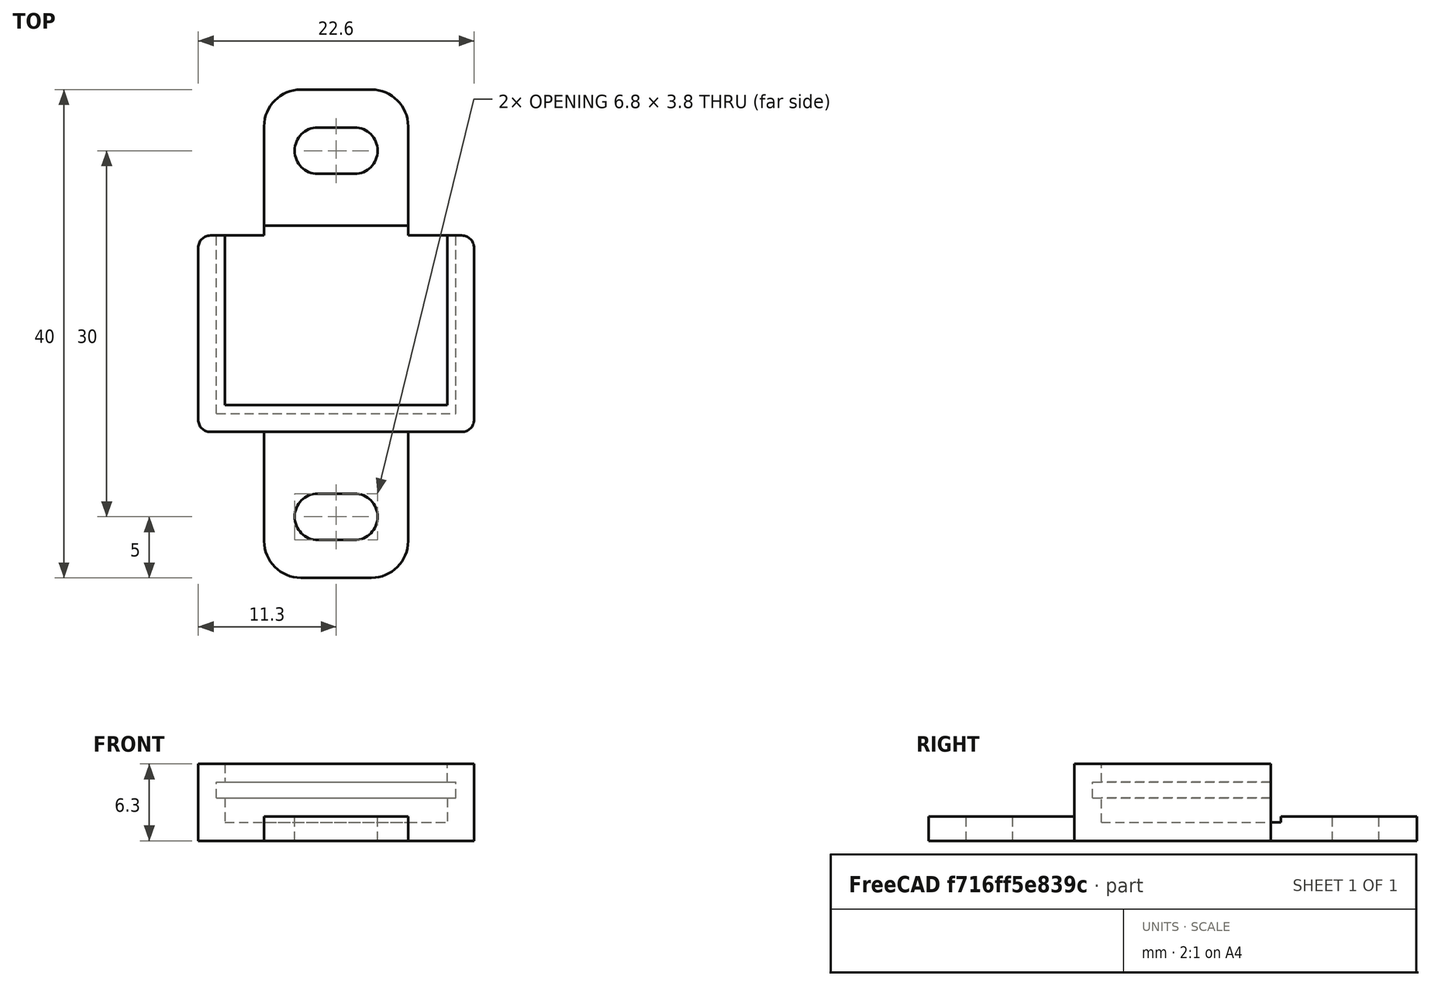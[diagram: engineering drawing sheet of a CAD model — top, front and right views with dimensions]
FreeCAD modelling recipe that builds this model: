
FCSTD DOCUMENT  (FreeCAD 0.19R23578 (Git))
Label: charger_s09
License: FreeArt
LicenseURL: http://artlibre.org/licence/lal
objects: Part::Box×3, Part::MultiFuse×2, Spreadsheet::Sheet×1, Part::Fillet×1, Part::Feature×1, Part::Cut×1, App::Part×1
note: 8 computed .brp shape members not serialized (recipe doc carries the construction recipe); baked Part::Feature solids carry a one-line shape summary decoded from their .brp

FEATURE [Spreadsheet::Sheet] Spreadsheet  label="p"
  cells = A1=pcb_x; B1(pcb_x)=19.6; A2=pcb_y; B2(pcb_y)=14.6; A3=pcb_z; B3(pcb_z)=1.3; A4=pcb_under; B4(pcb_under)=2; A5=side_wall; B5(side_wall)=1.5; A6=pcb_side_lane; B6(pcb_side_lane)=0.7; A7=bottom_wall; B7(bottom_wall)=1.5; A8=pcb_above; B8(pcb_above)=1.5
FEATURE [Part::Box] Box  label="external cube"
  AttacherType = Attacher::AttachEngine3D
  Height = 6.3
  Length = 22.6
  Width = 16.1
  expr: Length = <<p>>.pcb_x + 2 * <<p>>.side_wall
  expr: Width = <<p>>.pcb_y + <<p>>.side_wall
  expr: Height = <<p>>.bottom_wall + <<p>>.pcb_under + <<p>>.pcb_z + <<p>>.pcb_above
FEATURE [Part::Box] Box006  label="internal cube"
  AttacherType = Attacher::AttachEngine3D
  Height = 4.8
  Length = 18.2
  Placement = pos=(2.2,2.2,1.5) rot=(0,0,1;0rad)
  Width = 14.7
  expr: Length = <<p>>.pcb_x - 2 * <<p>>.pcb_side_lane
  expr: Width = <<p>>.pcb_y - 2 * <<p>>.pcb_side_lane + <<p>>.side_wall
  expr: Height = <<p>>.pcb_under + <<p>>.pcb_z + <<p>>.pcb_above
  expr: .Placement.Base.z = <<p>>.bottom_wall
  expr: .Placement.Base.x = <<p>>.side_wall + <<p>>.pcb_side_lane
  expr: .Placement.Base.y = <<p>>.side_wall + <<p>>.pcb_side_lane
FEATURE [Part::Box] Box007  label="pcb extract cube"
  AttacherType = Attacher::AttachEngine3D
  Height = 1.3
  Length = 19.6
  Placement = pos=(1.5,1.5,3.5) rot=(0,0,1;0rad)
  Width = 14.6
  expr: Height = <<p>>.pcb_z
  expr: .Placement.Base.z = <<p>>.bottom_wall + <<p>>.pcb_under
  expr: Width = <<p>>.pcb_y
  expr: Length = <<p>>.pcb_x
  expr: .Placement.Base.x = <<p>>.side_wall
  expr: .Placement.Base.y = <<p>>.side_wall
FEATURE [Part::MultiFuse] Fusion  label="extract fusion"
  Shapes = -> [Box006,Box007]
FEATURE [Part::Fillet] Fillet  label="external fillet"
  Base = -> Box
  Edges = 4 edges r=1: [Edge1,Edge3,Edge5,Edge7]
FEATURE [Part::Feature] Cut002002  label="attach plane y dir002"
  Placement = pos=(5.4,-11.95,0) rot=(0,0,1;0rad)
  shape: bbox 11.8 x 40 x 2 mm, 20 faces (baked)
FEATURE [Part::MultiFuse] Fusion001  label="body fusion"
  Shapes = -> [Fillet,Cut002002]
FEATURE [Part::Cut] Cut  label="body cut"
  Base = -> Fusion001
  Tool = -> Fusion
FEATURE [App::Part] Part  label="charger_s09 pcb box part"
  Group = -> [Box,Fillet,Fusion001,Fusion,Box007,Box006,Cut]
  Origin = -> Origin
